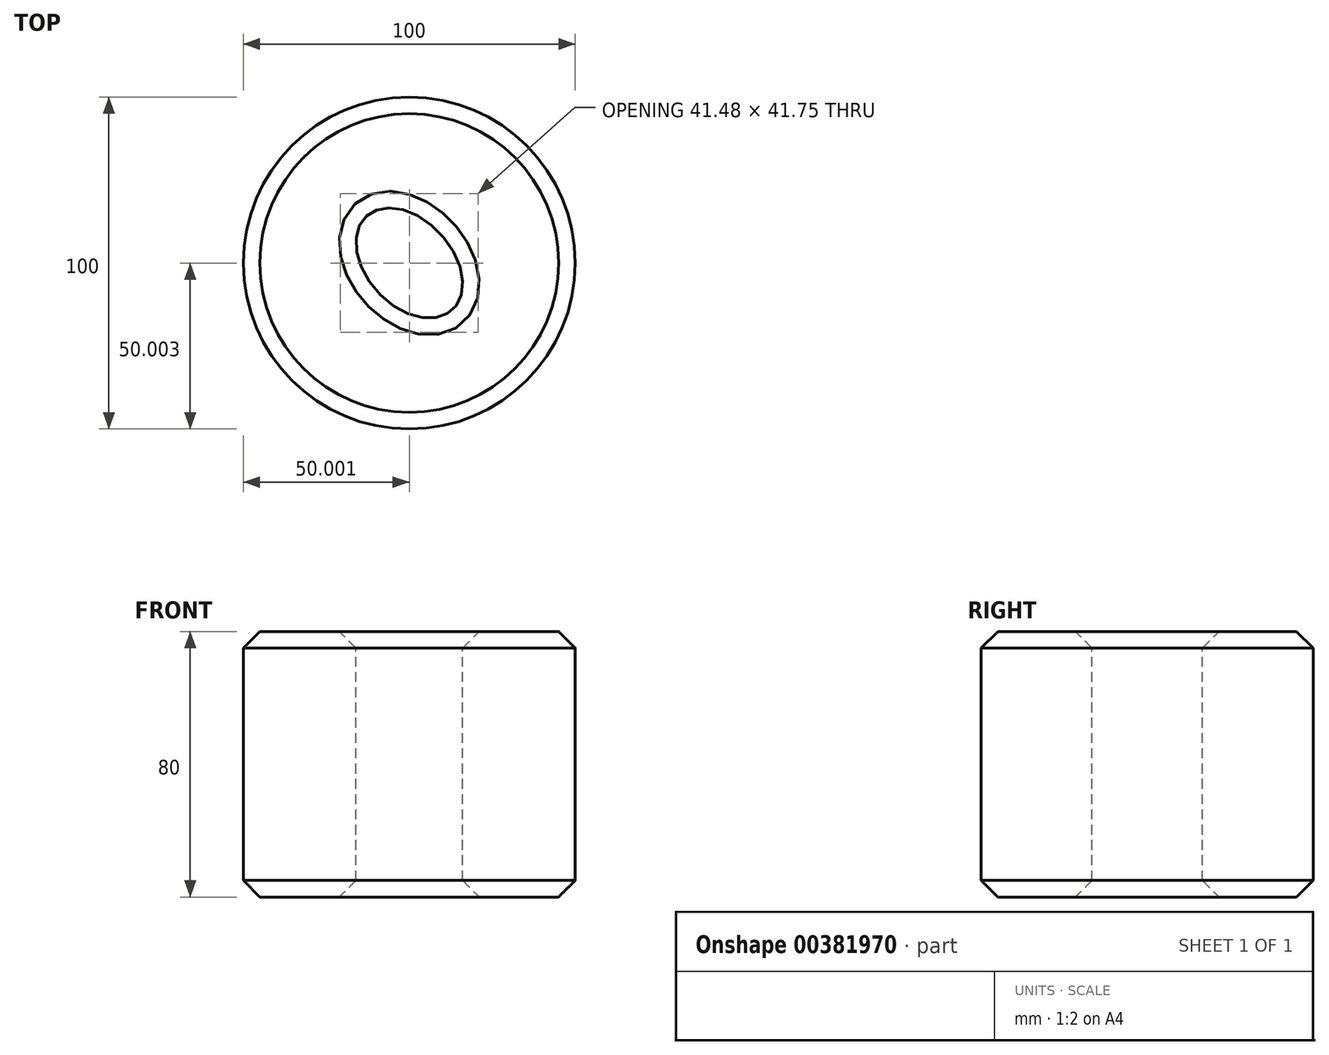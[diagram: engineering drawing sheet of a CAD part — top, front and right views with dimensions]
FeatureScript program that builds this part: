
annotation { "Feature Type Name" : "Feature", "Feature Type Description" : "" }
export const myFeature = defineFeature(function(context is Context, id is Id, definition is map)
    precondition{}
    {
        {
            var Q0;
            Q0=qCreatedBy(makeId("Top.planeOp"),FACE);
            var sketch = newSketch(context, id + "F0", { "sketchPlane" : qUnion([Q0])});
            skCircle(sketch, "E0", {"center": v(0, 0) * mm, "radius": 50 * mm});
            skSolve(sketch);
        }
        {
            var Q0;
            Q0=makeQuery(id+"F0.imprint","IMPRINT",FACE,{"disambiguationData":[TD([[makeQuery(id+"F0.imprint","IMPRINT",EDGE,{"derivedFrom":sQuery(id+"F0.wireOp",EDGE,"E0")}),1.0]])]});
            extrude(context, id + "F1", {"entities" : qUnion([Q0]), "depth" : 80 * mm});
        }
        {
            var Q0;
            Q0=qCreatedBy(makeId("Top.planeOp"),FACE);
            var sketch = newSketch(context, id + "F2", { "sketchPlane" : qUnion([Q0])});
            skEllipse(sketch, "E1", {"center": v(0, 0) * mm, "majorRadius": 19.18 * mm, "minorRadius": 12.92 * mm, "majorAxis": v(-0.67, 0.74)});
            skSolve(sketch);
        }
        {
            var Q0;
            Q0 = qSketchRegion(id + "F2", true);
            extrude(context, id + "F3", {"entities" : qUnion([Q0]), "operationType" : NewBodyOperationType.REMOVE, "endBound" : BoundingType.THROUGH_ALL, "depth" : 25 * mm});
        }
        {
            var Q0;
            Q0=makeQuery(id+"F1.opExtrude","SWEPT_FACE",FACE,{"disambiguationData":[OSD([sQuery(id+"F0.wireOp",EDGE,"E0")])]});
            var Q1;
            Q1=makeQuery(id+"F1.opExtrude","CAP_FACE",FACE,{"disambiguationData":[OSD([sQuery(id+"F0.wireOp",EDGE,"E0")])],"isStart":false});
            var Q2;
            Q2=makeQuery(id+"F3.boolean.opBoolean","COPY",FACE,{"derivedFrom":makeQuery(id+"F3.opExtrude","SWEPT_FACE",FACE,{"disambiguationData":[OSD([sQuery(id+"F2.wireOp",EDGE,"E1")])]})});
            chamfer(context, id + "F4", {"entities" : qUnion([Q0, Q1, Q2]), "chamferType" : ChamferType.TWO_OFFSETS, "width1" : 5 * mm, "oppositeDirection" : false, "width2" : 5 * mm, "tangentPropagation" : true});
        }
    });
